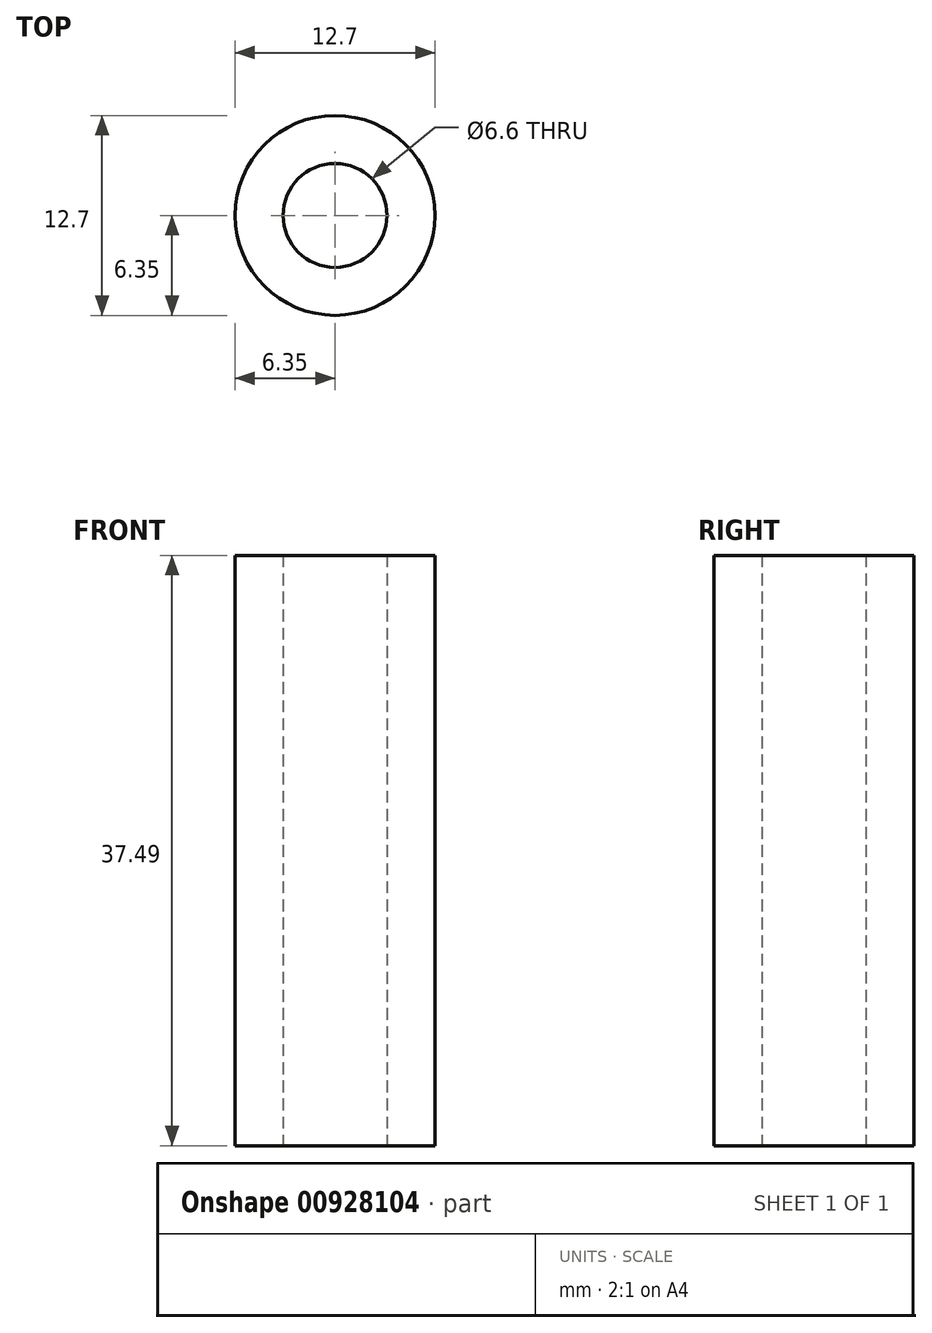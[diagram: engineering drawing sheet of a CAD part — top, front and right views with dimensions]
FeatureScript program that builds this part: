
annotation { "Feature Type Name" : "Feature", "Feature Type Description" : "" }
export const myFeature = defineFeature(function(context is Context, id is Id, definition is map)
    precondition{}
    {
        {
            var Q0;
            Q0=qCreatedBy(makeId("Top.planeOp"),FACE);
            var sketch = newSketch(context, id + "F0", { "sketchPlane" : qUnion([Q0])});
            skCircle(sketch, "E0", {"center": v(0, 0) * mm, "radius": 6.35 * mm});
            skCircle(sketch, "E1", {"center": v(0, 0) * mm, "radius": 3.3 * mm});
            skSolve(sketch);
        }
        {
            var Q0;
            Q0=qSketchRegion(id+"F0",true);
            extrude(context, id + "F1", {"entities" : qUnion([Q0]), "depth" : 37.5 * mm, "offsetDistance" : 25.4 * mm});
        }
    });
